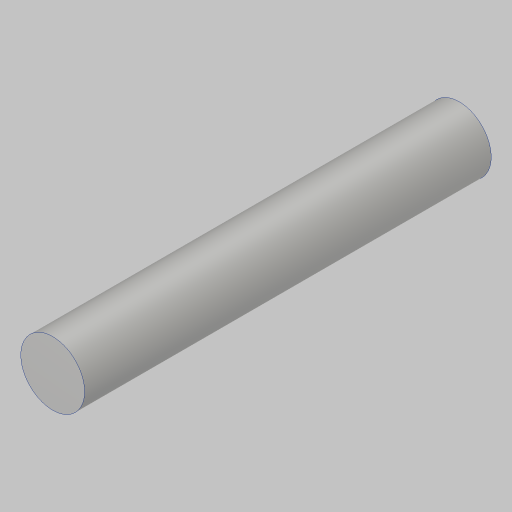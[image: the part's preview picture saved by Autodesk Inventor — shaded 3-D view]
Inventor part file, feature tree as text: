
AUTODESK INVENTOR PART (.ipt)
format: ipt  version: 2023.5 (Build 275446000, 446)  size: 89,600 bytes
history: native  units: in
note: dims shown in document units (in); Inventor stores cm internally (conversion verified against a paired STEP export)
features: extrude x1, sketch x1
ambient origin geometry x8: Origin, YZ Plane, XZ Plane, XY Plane, X Axis, Y Axis, Z Axis, Center Point
bodies: Solid1 (feature_tree)
feature tree (2):
  extrude  "Extrusion1"  Depth=2.0079in TaperAngle=0.0deg
  sketch  "Sketch1"  dims[d0=0.315in d1=2.0079in d2=0.0in]
